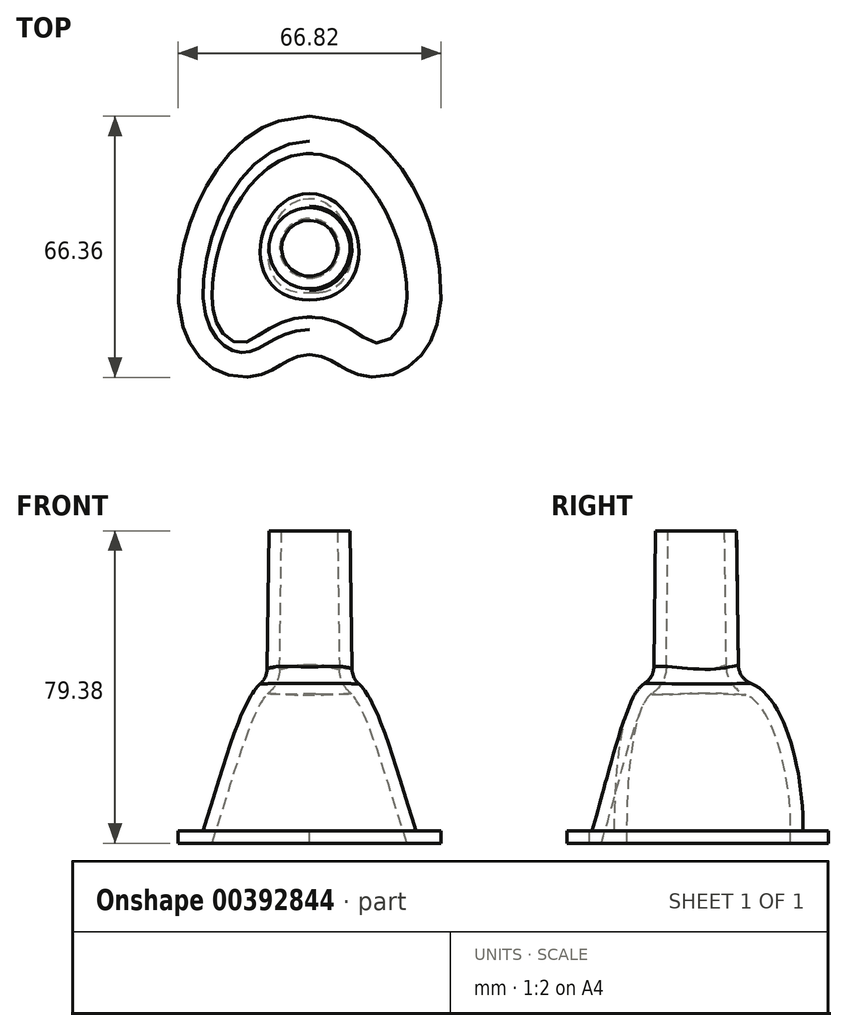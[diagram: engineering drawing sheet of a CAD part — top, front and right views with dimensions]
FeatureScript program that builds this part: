
annotation { "Feature Type Name" : "Feature", "Feature Type Description" : "" }
export const myFeature = defineFeature(function(context is Context, id is Id, definition is map)
    precondition{}
    {
        {
            var Q0;
            Q0=qCreatedBy(makeId("Top.planeOp"),FACE);
            cPlane(context, id + "F0", {"entities" : qUnion([Q0]), "cplaneType" : CPlaneType.OFFSET, "offset" : 76.2 * mm, "width" : 152.4 * mm, "height" : 152.4 * mm});
        }
        {
            var Q0;
            Q0=qCreatedBy(id+"F0.planeOp",FACE);
            var sketch = newSketch(context, id + "F1", { "sketchPlane" : qUnion([Q0])});
            skCircle(sketch, "E0", {"center": v(0, 0) * mm, "radius": 10.29 * mm});
            skSolve(sketch);
        }
        {
            var Q0;
            Q0=qCreatedBy(makeId("Top.planeOp"),FACE);
            cPlane(context, id + "F2", {"entities" : qUnion([Q0]), "cplaneType" : CPlaneType.OFFSET, "offset" : 38.1 * mm, "width" : 152.4 * mm, "height" : 152.4 * mm});
        }
        {
            var Q0;
            Q0=qCreatedBy(id+"F2.planeOp",FACE);
            var sketch = newSketch(context, id + "F3", { "sketchPlane" : qUnion([Q0])});
            skCircle(sketch, "E1", {"center": v(0, 0) * mm, "radius": 10.8 * mm});
            skSolve(sketch);
        }
        {
            var Q0;
            Q0=qCreatedBy(makeId("Top.planeOp"),FACE);
            var sketch = newSketch(context, id + "F4", { "sketchPlane" : qUnion([Q0])});
            skFitSpline(sketch, "E2", {"points": [v(0, 27.2) * mm, v(-26.53, -16.48) * mm, v(-15.51, -26.34) * mm, v(0, -20.7) * mm], "startDerivative": vector(-124.35, 0) * mm, "endDerivative": vector(87.79, 0) * mm});
            skLineSegment(sketch, "E3", {"start": v(0, 27.2) * mm, "end": v(-39.36, 27.2) * mm, "construction": true});
            skLineSegment(sketch, "E4", {"start": v(0, -20.7) * mm, "end": v(-44.27, -20.7) * mm, "construction": true});
            skFitSpline(sketch, "E5.MirrorCS", {"points": [v(0, 27.2) * mm, v(26.53, -16.48) * mm, v(15.51, -26.34) * mm, v(0, -20.7) * mm], "startDerivative": vector(124.35, 0) * mm, "endDerivative": vector(-87.79, 0) * mm});
            skSolve(sketch);
        }
        {
            var Q0;
            Q0=qCreatedBy(makeId("Right.planeOp"),FACE);
            var sketch = newSketch(context, id + "F5", { "sketchPlane" : qUnion([Q0])});
            skPoint(sketch, "E6.0", {"position": v(27.2, 0) * mm});
            skPoint(sketch, "E7.0", {"position": v(-20.7, 0) * mm});
            skLineSegment(sketch, "E8.0", {"start": v(-10.8, 38.1) * mm, "end": v(10.8, 38.1) * mm, "construction": true});
            skFitSpline(sketch, "E9", {"points": [v(10.8, 38.1) * mm, v(27.2, 0) * mm], "startDerivative": vector(31.94, 0) * mm, "endDerivative": vector(0, -52.58) * mm});
            skLineSegment(sketch, "E10", {"start": v(10.8, 38.1) * mm, "end": v(21.44, 38.1) * mm, "construction": true});
            skLineSegment(sketch, "E11", {"start": v(-10.8, 38.1) * mm, "end": v(-18.53, 38.1) * mm, "construction": true});
            skLineSegment(sketch, "E12", {"start": v(27.2, 0) * mm, "end": v(27.2, 17.53) * mm, "construction": true});
            skPoint(sketch, "E13", {"position": v(16.12, 38.1) * mm});
            skFitSpline(sketch, "E14", {"points": [v(-10.8, 38.1) * mm, v(-20.7, 0) * mm], "startDerivative": vector(-23.2, 0) * mm, "endDerivative": vector(0, -52.58) * mm});
            skLineSegment(sketch, "E15", {"start": v(-20.7, 0) * mm, "end": v(-20.7, 17.53) * mm, "construction": true});
            skSolve(sketch);
        }
        {
            var Q0;
            Q0=makeQuery(id+"F3.imprint","IMPRINT",FACE,{"disambiguationData":[TD([[makeQuery(id+"F3.imprint","IMPRINT",EDGE,{"derivedFrom":sQuery(id+"F3.wireOp",EDGE,"E1")}),1.0]])]});
            var Q1;
            Q1=makeQuery(id+"F4.imprint","IMPRINT",FACE,{"disambiguationData":[TD([[makeQuery(id+"F4.imprint","IMPRINT",EDGE,{"derivedFrom":sQuery(id+"F4.wireOp",EDGE,"E2")}),1.0]])]});
            var Q2;
            Q2=sQuery(id+"F5.wireOp",EDGE,"E9");
            var Q3;
            Q3=sQuery(id+"F5.wireOp",EDGE,"E14");
            loft(context, id + "F6", {"addGuides" : true, "sheetProfilesArray" : [{ "sheetProfileEntities" : qUnion([Q0]) }, { "sheetProfileEntities" : qUnion([Q1]) }], "guidesArray" : [{ "guideEntities" : qUnion([Q2]), "guideDerivativeType" : LoftGuideDerivativeType.DEFAULT, "guideDerivativeMagnitude" : 1 }, { "guideEntities" : qUnion([Q3]), "guideDerivativeType" : LoftGuideDerivativeType.DEFAULT, "guideDerivativeMagnitude" : 1 }]});
        }
        {
            var Q0;
            Q0=qCreatedBy(makeId("Top.planeOp"),FACE);
            var sketch = newSketch(context, id + "F7", { "sketchPlane" : qUnion([Q0])});
            skFitSpline(sketch, "E16.0", {"points": [v(0, -27.04) * mm, v(-0.15, -27.04) * mm, v(-0.43, -27.05) * mm, v(-0.85, -27.07) * mm, v(-1.18, -27.1) * mm, v(-1.41, -27.13) * mm, v(-1.54, -27.15) * mm, v(-1.64, -27.16) * mm, v(-1.73, -27.17) * mm, v(-1.84, -27.2) * mm, v(-2.04, -27.23) * mm, v(-2.33, -27.28) * mm, v(-2.61, -27.35) * mm, v(-2.8, -27.4) * mm, v(-2.92, -27.44) * mm, v(-3, -27.46) * mm, v(-3.08, -27.48) * mm, v(-3.18, -27.51) * mm, v(-3.36, -27.57) * mm, v(-3.56, -27.64) * mm, v(-3.77, -27.72) * mm, v(-3.93, -27.78) * mm, v(-4.07, -27.84) * mm, v(-4.16, -27.88) * mm, v(-4.21, -27.9) * mm, v(-4.26, -27.92) * mm, v(-4.3, -27.93) * mm, v(-4.34, -27.95) * mm, v(-4.42, -28) * mm, v(-4.6, -28.07) * mm, v(-4.8, -28.16) * mm, v(-5, -28.27) * mm, v(-5.15, -28.34) * mm, v(-5.26, -28.4) * mm, v(-5.35, -28.45) * mm, v(-5.42, -28.48) * mm, v(-5.47, -28.51) * mm, v(-5.5, -28.53) * mm, v(-5.52, -28.54) * mm, v(-5.54, -28.55) * mm, v(-5.56, -28.56) * mm, v(-5.6, -28.58) * mm, v(-5.65, -28.6) * mm, v(-5.72, -28.65) * mm, v(-5.82, -28.7) * mm, v(-5.95, -28.77) * mm, v(-6.11, -28.87) * mm, v(-6.3, -28.97) * mm, v(-6.48, -29.08) * mm, v(-6.65, -29.18) * mm, v(-6.77, -29.25) * mm, v(-6.84, -29.3) * mm, v(-6.9, -29.33) * mm, v(-6.94, -29.35) * mm, v(-7, -29.4) * mm, v(-7.11, -29.45) * mm, v(-7.27, -29.55) * mm, v(-7.42, -29.64) * mm, v(-7.53, -29.7) * mm, v(-7.6, -29.74) * mm, v(-7.64, -29.77) * mm, v(-7.69, -29.8) * mm, v(-7.76, -29.84) * mm, v(-7.88, -29.91) * mm, v(-8.05, -30.02) * mm, v(-8.23, -30.12) * mm, v(-8.35, -30.19) * mm, v(-8.42, -30.23) * mm, v(-8.46, -30.26) * mm, v(-8.53, -30.3) * mm, v(-8.6, -30.34) * mm, v(-8.71, -30.4) * mm, v(-8.83, -30.46) * mm, v(-9, -30.55) * mm, v(-9.19, -30.66) * mm, v(-9.42, -30.8) * mm, v(-9.66, -30.91) * mm, v(-9.85, -31.01) * mm, v(-10, -31.1) * mm, v(-10.12, -31.15) * mm, v(-10.22, -31.2) * mm, v(-10.29, -31.23) * mm, v(-10.32, -31.25) * mm, v(-10.35, -31.26) * mm, v(-10.39, -31.28) * mm, v(-10.44, -31.3) * mm, v(-10.52, -31.34) * mm, v(-10.64, -31.4) * mm, v(-10.78, -31.46) * mm, v(-10.97, -31.55) * mm, v(-11.2, -31.65) * mm, v(-11.5, -31.77) * mm, v(-11.8, -31.88) * mm, v(-12.1, -31.99) * mm, v(-12.34, -32.08) * mm, v(-12.52, -32.13) * mm, v(-12.62, -32.16) * mm, v(-12.7, -32.19) * mm, v(-12.78, -32.21) * mm, v(-12.9, -32.25) * mm, v(-13.1, -32.3) * mm, v(-13.39, -32.38) * mm, v(-13.74, -32.47) * mm, v(-14.2, -32.57) * mm, v(-14.68, -32.65) * mm, v(-15.17, -32.7) * mm, v(-15.53, -32.74) * mm, v(-15.9, -32.77) * mm, v(-16.4, -32.8) * mm, v(-17.01, -32.8) * mm, v(-17.62, -32.77) * mm, v(-18.11, -32.72) * mm, v(-18.48, -32.68) * mm, v(-18.85, -32.63) * mm, v(-19.34, -32.55) * mm, v(-19.94, -32.42) * mm, v(-20.54, -32.27) * mm, v(-21.02, -32.12) * mm, v(-21.36, -32) * mm, v(-21.72, -31.88) * mm, v(-22.2, -31.7) * mm, v(-22.77, -31.45) * mm, v(-23.34, -31.17) * mm, v(-23.72, -30.96) * mm, v(-23.94, -30.84) * mm, v(-24.1, -30.74) * mm, v(-24.27, -30.64) * mm, v(-24.5, -30.5) * mm, v(-24.87, -30.27) * mm, v(-25.4, -29.9) * mm, v(-25.92, -29.5) * mm, v(-26.27, -29.22) * mm, v(-26.46, -29.05) * mm, v(-26.6, -28.93) * mm, v(-26.76, -28.8) * mm, v(-26.95, -28.62) * mm, v(-27.3, -28.3) * mm, v(-27.76, -27.82) * mm, v(-28.2, -27.32) * mm, v(-28.5, -26.97) * mm, v(-28.67, -26.76) * mm, v(-28.8, -26.6) * mm, v(-28.92, -26.44) * mm, v(-29.09, -26.22) * mm, v(-29.38, -25.83) * mm, v(-29.76, -25.25) * mm, v(-30.13, -24.67) * mm, v(-30.37, -24.25) * mm, v(-30.5, -24) * mm, v(-30.6, -23.82) * mm, v(-30.7, -23.63) * mm, v(-30.83, -23.37) * mm, v(-31.06, -22.92) * mm, v(-31.36, -22.26) * mm, v(-31.63, -21.59) * mm, v(-31.8, -21.1) * mm, v(-31.9, -20.83) * mm, v(-31.97, -20.63) * mm, v(-32.05, -20.41) * mm, v(-32.14, -20.12) * mm, v(-32.3, -19.61) * mm, v(-32.5, -18.88) * mm, v(-32.71, -17.98) * mm, v(-32.9, -17.08) * mm, v(-33.04, -16.15) * mm, v(-33.17, -15.21) * mm, v(-33.26, -14.26) * mm, v(-33.33, -13.28) * mm, v(-33.38, -12.31) * mm, v(-33.4, -11) * mm, v(-33.38, -9.33) * mm, v(-33.25, -7.29) * mm, v(-33.08, -5.57) * mm, v(-32.9, -4.16) * mm, v(-32.73, -3.1) * mm, v(-32.58, -2.23) * mm, v(-32.45, -1.52) * mm, v(-32.34, -1) * mm, v(-32.23, -0.46) * mm, v(-32.08, 0.26) * mm, v(-31.87, 1.15) * mm, v(-31.65, 2.04) * mm, v(-31.46, 2.75) * mm, v(-31.31, 3.28) * mm, v(-31.16, 3.82) * mm, v(-30.95, 4.54) * mm, v(-30.67, 5.44) * mm, v(-30.38, 6.32) * mm, v(-30.16, 6.94) * mm, v(-30.04, 7.3) * mm, v(-29.94, 7.56) * mm, v(-29.85, 7.83) * mm, v(-29.71, 8.18) * mm, v(-29.48, 8.8) * mm, v(-29.13, 9.7) * mm, v(-28.76, 10.56) * mm, v(-28.5, 11.17) * mm, v(-28.35, 11.52) * mm, v(-28.23, 11.77) * mm, v(-28.1, 12.04) * mm, v(-27.95, 12.39) * mm, v(-27.66, 13) * mm, v(-27.24, 13.85) * mm, v(-26.8, 14.7) * mm, v(-26.48, 15.28) * mm, v(-26.3, 15.61) * mm, v(-26.16, 15.86) * mm, v(-26.02, 16.11) * mm, v(-25.82, 16.45) * mm, v(-25.48, 17.03) * mm, v(-24.98, 17.85) * mm, v(-24.47, 18.66) * mm, v(-24.1, 19.2) * mm, v(-23.88, 19.52) * mm, v(-23.72, 19.75) * mm, v(-23.55, 20) * mm, v(-23.33, 20.3) * mm, v(-22.93, 20.86) * mm, v(-22.34, 21.62) * mm, v(-21.74, 22.37) * mm, v(-21.32, 22.88) * mm, v(-21.07, 23.17) * mm, v(-20.88, 23.38) * mm, v(-20.69, 23.6) * mm, v(-20.43, 23.89) * mm, v(-19.97, 24.39) * mm, v(-19.3, 25.08) * mm, v(-18.6, 25.75) * mm, v(-18.11, 26.2) * mm, v(-17.83, 26.46) * mm, v(-17.62, 26.64) * mm, v(-17.4, 26.84) * mm, v(-17.1, 27.1) * mm, v(-16.56, 27.53) * mm, v(-15.8, 28.13) * mm, v(-15, 28.7) * mm, v(-14.45, 29.08) * mm, v(-14.13, 29.3) * mm, v(-13.89, 29.45) * mm, v(-13.63, 29.6) * mm, v(-13.3, 29.81) * mm, v(-12.7, 30.17) * mm, v(-12, 30.55) * mm, v(-11.3, 30.9) * mm, v(-10.76, 31.16) * mm, v(-10.3, 31.37) * mm, v(-10, 31.5) * mm, v(-9.8, 31.58) * mm, v(-9.68, 31.64) * mm, v(-9.53, 31.7) * mm, v(-9.34, 31.77) * mm, v(-9, 31.9) * mm, v(-8.51, 32.09) * mm, v(-7.93, 32.29) * mm, v(-7.14, 32.54) * mm, v(-6.14, 32.81) * mm, v(-4.53, 33.18) * mm, v(-2.48, 33.48) * mm, v(-0.83, 33.56) * mm, v(0, 33.56) * mm]});
            skFitSpline(sketch, "E16.1", {"points": [v(0, 33.56) * mm, v(0.83, 33.56) * mm, v(2.48, 33.48) * mm, v(4.53, 33.18) * mm, v(6.14, 32.81) * mm, v(7.14, 32.54) * mm, v(7.93, 32.29) * mm, v(8.51, 32.09) * mm, v(9, 31.9) * mm, v(9.34, 31.77) * mm, v(9.53, 31.7) * mm, v(9.67, 31.64) * mm, v(9.8, 31.58) * mm, v(10, 31.5) * mm, v(10.3, 31.37) * mm, v(10.76, 31.16) * mm, v(11.3, 30.9) * mm, v(12, 30.55) * mm, v(12.7, 30.17) * mm, v(13.3, 29.81) * mm, v(13.63, 29.6) * mm, v(13.89, 29.45) * mm, v(14.13, 29.3) * mm, v(14.45, 29.08) * mm, v(15, 28.7) * mm, v(15.8, 28.13) * mm, v(16.56, 27.53) * mm, v(17.1, 27.1) * mm, v(17.4, 26.84) * mm, v(17.62, 26.64) * mm, v(17.83, 26.46) * mm, v(18.11, 26.2) * mm, v(18.6, 25.75) * mm, v(19.3, 25.08) * mm, v(19.97, 24.39) * mm, v(20.43, 23.89) * mm, v(20.69, 23.6) * mm, v(20.88, 23.38) * mm, v(21.07, 23.17) * mm, v(21.32, 22.88) * mm, v(21.74, 22.37) * mm, v(22.34, 21.62) * mm, v(22.93, 20.86) * mm, v(23.33, 20.3) * mm, v(23.55, 20) * mm, v(23.72, 19.75) * mm, v(23.88, 19.52) * mm, v(24.1, 19.2) * mm, v(24.47, 18.66) * mm, v(24.98, 17.85) * mm, v(25.48, 17.03) * mm, v(25.82, 16.45) * mm, v(26.02, 16.11) * mm, v(26.16, 15.86) * mm, v(26.3, 15.61) * mm, v(26.48, 15.28) * mm, v(26.8, 14.7) * mm, v(27.24, 13.85) * mm, v(27.66, 13) * mm, v(27.95, 12.39) * mm, v(28.1, 12.04) * mm, v(28.23, 11.77) * mm, v(28.35, 11.52) * mm, v(28.5, 11.17) * mm, v(28.76, 10.57) * mm, v(29.13, 9.7) * mm, v(29.48, 8.8) * mm, v(29.71, 8.19) * mm, v(29.85, 7.83) * mm, v(29.94, 7.56) * mm, v(30.04, 7.3) * mm, v(30.16, 6.94) * mm, v(30.38, 6.32) * mm, v(30.67, 5.44) * mm, v(30.95, 4.54) * mm, v(31.16, 3.82) * mm, v(31.31, 3.28) * mm, v(31.46, 2.75) * mm, v(31.65, 2.04) * mm, v(31.87, 1.15) * mm, v(32.08, 0.26) * mm, v(32.23, -0.46) * mm, v(32.34, -1) * mm, v(32.45, -1.52) * mm, v(32.58, -2.23) * mm, v(32.73, -3.1) * mm, v(32.9, -4.16) * mm, v(33.03, -5.21) * mm, v(33.15, -6.25) * mm, v(33.28, -7.63) * mm, v(33.38, -9.33) * mm, v(33.4, -11) * mm, v(33.38, -12.31) * mm, v(33.33, -13.28) * mm, v(33.26, -14.26) * mm, v(33.17, -15.2) * mm, v(33.04, -16.15) * mm, v(32.9, -17.08) * mm, v(32.71, -17.98) * mm, v(32.5, -18.88) * mm, v(32.3, -19.61) * mm, v(32.14, -20.12) * mm, v(32.05, -20.41) * mm, v(31.97, -20.63) * mm, v(31.9, -20.83) * mm, v(31.8, -21.1) * mm, v(31.63, -21.58) * mm, v(31.36, -22.26) * mm, v(31.06, -22.92) * mm, v(30.83, -23.37) * mm, v(30.7, -23.63) * mm, v(30.6, -23.82) * mm, v(30.5, -24) * mm, v(30.37, -24.24) * mm, v(30.13, -24.66) * mm, v(29.76, -25.25) * mm, v(29.38, -25.83) * mm, v(29.09, -26.22) * mm, v(28.92, -26.44) * mm, v(28.8, -26.6) * mm, v(28.67, -26.76) * mm, v(28.5, -26.97) * mm, v(28.2, -27.32) * mm, v(27.76, -27.82) * mm, v(27.3, -28.3) * mm, v(26.95, -28.61) * mm, v(26.76, -28.8) * mm, v(26.6, -28.93) * mm, v(26.46, -29.05) * mm, v(26.27, -29.22) * mm, v(25.92, -29.5) * mm, v(25.4, -29.9) * mm, v(24.87, -30.27) * mm, v(24.5, -30.5) * mm, v(24.27, -30.64) * mm, v(24.1, -30.74) * mm, v(23.94, -30.84) * mm, v(23.72, -30.96) * mm, v(23.34, -31.17) * mm, v(22.77, -31.45) * mm, v(22.2, -31.7) * mm, v(21.72, -31.88) * mm, v(21.37, -32) * mm, v(21.02, -32.12) * mm, v(20.54, -32.27) * mm, v(19.95, -32.42) * mm, v(19.22, -32.57) * mm, v(18.48, -32.69) * mm, v(17.75, -32.76) * mm, v(17.01, -32.8) * mm, v(16.4, -32.8) * mm, v(15.9, -32.77) * mm, v(15.53, -32.74) * mm, v(15.17, -32.7) * mm, v(14.69, -32.65) * mm, v(14.2, -32.57) * mm, v(13.74, -32.47) * mm, v(13.39, -32.38) * mm, v(13.1, -32.3) * mm, v(12.9, -32.25) * mm, v(12.78, -32.21) * mm, v(12.7, -32.19) * mm, v(12.62, -32.16) * mm, v(12.52, -32.13) * mm, v(12.34, -32.08) * mm, v(12.1, -31.99) * mm, v(11.8, -31.88) * mm, v(11.5, -31.77) * mm, v(11.21, -31.65) * mm, v(10.97, -31.55) * mm, v(10.78, -31.46) * mm, v(10.64, -31.4) * mm, v(10.52, -31.34) * mm, v(10.44, -31.3) * mm, v(10.39, -31.28) * mm, v(10.35, -31.26) * mm, v(10.33, -31.25) * mm, v(10.29, -31.23) * mm, v(10.22, -31.2) * mm, v(10.12, -31.15) * mm, v(10, -31.1) * mm, v(9.85, -31.01) * mm, v(9.66, -30.91) * mm, v(9.42, -30.8) * mm, v(9.19, -30.66) * mm, v(9, -30.55) * mm, v(8.83, -30.47) * mm, v(8.71, -30.4) * mm, v(8.6, -30.34) * mm, v(8.54, -30.3) * mm, v(8.5, -30.28) * mm, v(8.46, -30.26) * mm, v(8.45, -30.24) * mm, v(8.41, -30.23) * mm, v(8.36, -30.2) * mm, v(8.28, -30.15) * mm, v(8.19, -30.1) * mm, v(8.05, -30.02) * mm, v(7.91, -29.93) * mm, v(7.78, -29.86) * mm, v(7.72, -29.82) * mm, v(7.68, -29.8) * mm, v(7.65, -29.78) * mm, v(7.63, -29.76) * mm, v(7.6, -29.74) * mm, v(7.54, -29.7) * mm, v(7.46, -29.66) * mm, v(7.36, -29.6) * mm, v(7.23, -29.53) * mm, v(7.07, -29.43) * mm, v(6.92, -29.34) * mm, v(6.78, -29.26) * mm, v(6.65, -29.18) * mm, v(6.43, -29.05) * mm, v(6.2, -28.91) * mm, v(5.97, -28.79) * mm, v(5.84, -28.71) * mm, v(5.74, -28.66) * mm, v(5.66, -28.62) * mm, v(5.6, -28.58) * mm, v(5.56, -28.56) * mm, v(5.52, -28.54) * mm, v(5.48, -28.51) * mm, v(5.42, -28.48) * mm, v(5.32, -28.43) * mm, v(5.18, -28.36) * mm, v(5.01, -28.27) * mm, v(4.8, -28.17) * mm, v(4.6, -28.07) * mm, v(4.42, -28) * mm, v(4.34, -27.95) * mm, v(4.29, -27.93) * mm, v(4.26, -27.92) * mm, v(4.21, -27.9) * mm, v(4.16, -27.88) * mm, v(4.07, -27.84) * mm, v(3.93, -27.78) * mm, v(3.77, -27.72) * mm, v(3.56, -27.64) * mm, v(3.36, -27.57) * mm, v(3.18, -27.51) * mm, v(3.08, -27.48) * mm, v(3, -27.46) * mm, v(2.92, -27.44) * mm, v(2.8, -27.4) * mm, v(2.61, -27.35) * mm, v(2.33, -27.28) * mm, v(2.04, -27.23) * mm, v(1.84, -27.2) * mm, v(1.72, -27.17) * mm, v(1.64, -27.16) * mm, v(1.54, -27.15) * mm, v(1.41, -27.13) * mm, v(1.18, -27.1) * mm, v(0.85, -27.07) * mm, v(0.43, -27.05) * mm, v(0.15, -27.04) * mm, v(0, -27.04) * mm]});
            skSolve(sketch);
        }
        {
            var Q0;
            Q0 = qSketchRegion(id + "F7", true);
            extrude(context, id + "F8", {"entities" : qUnion([Q0]), "operationType" : NewBodyOperationType.ADD, "oppositeDirection" : true, "depth" : 3.17 * mm});
        }
        {
            var Q1;
            Q1=makeQuery(id+"F1.imprint","IMPRINT",FACE,{"disambiguationData":[TD([[makeQuery(id+"F1.imprint","IMPRINT",EDGE,{"derivedFrom":sQuery(id+"F1.wireOp",EDGE,"E0")}),1.0]])]});
            var Q2;
            Q2=makeQuery(id+"F6.opLoft","CAP_FACE",FACE,{"disambiguationData":[OSD([makeQuery(id+"F3.imprint","IMPRINT",FACE,{"disambiguationData":[TD([[makeQuery(id+"F3.imprint","IMPRINT",EDGE,{"derivedFrom":sQuery(id+"F3.wireOp",EDGE,"E1")}),1.0]])]})])],"isStart":true});
            loft(context, id + "F9", {"operationType" : NewBodyOperationType.ADD, "sheetProfilesArray" : [{ "sheetProfileEntities" : qUnion([Q1]) }, { "sheetProfileEntities" : qUnion([Q2]) }]});
        }
        {
            var Q0;
            Q0=makeQuery(id+"F6.opLoft","MID_CAP_EDGE",EDGE,{"disambiguationData":[OSD([sQuery(id+"F4.wireOp",EDGE,"E5.MirrorCS"),sQuery(id+"F5.wireOp",EDGE,"E9"),sQuery(id+"F5.wireOp",EDGE,"E14")])],"capPos":1.0});
            var Q1;
            {var subQ0=sQuery(id+"F5.wireOp",EDGE,"E14");var subQ1=sQuery(id+"F5.wireOp",EDGE,"E9");var subQ2=sQuery(id+"F3.wireOp",EDGE,"E1");var subQ3=makeQuery(id+"F6.opLoft","MID_CAP_EDGE",EDGE,{"disambiguationData":[OSD([subQ2,subQ1,subQ0]),OD(0.0)],"capPos":0.0});Q1=makeQuery(id+"F9.boolean.opBoolean","MERGE",EDGE,{"derivedFrom":[subQ3,makeQuery(id+"F9.opLoft","MID_CAP_EDGE",EDGE,{"disambiguationData":[OSD([subQ2,subQ1,subQ0]),TDD([makeQuery(id+"F6.opLoft","MID_CAP_VERTEX",VERTEX,{"disambiguationData":[OSD([subQ1])],"capPos":0.0}),makeQuery(id+"F6.opLoft","MID_CAP_VERTEX",VERTEX,{"disambiguationData":[OSD([subQ0])],"capPos":0.0}),subQ3])],"capPos":1.0})]});}
            fillet(context, id + "F10", {"entities" : qUnion([Q0, Q1]), "radius" : 5.08 * mm, "tangentPropagation" : true, "allowEdgeOverflow" : false});
        }
        {
            var Q0;
            Q0=makeQuery(id+"F8.opExtrude","CAP_FACE",FACE,{"disambiguationData":[OSD([sQuery(id+"F7.wireOp",EDGE,"E16.0"),sQuery(id+"F7.wireOp",EDGE,"E16.1")])],"isStart":false});
            var Q1;
            Q1=makeQuery(id+"F9.opLoft","CAP_FACE",FACE,{"disambiguationData":[OSD([makeQuery(id+"F1.imprint","IMPRINT",FACE,{"disambiguationData":[TD([[makeQuery(id+"F1.imprint","IMPRINT",EDGE,{"derivedFrom":sQuery(id+"F1.wireOp",EDGE,"E0")}),1.0]])]})])],"isStart":true});
            shell(context, id + "F11", {"entities" : qUnion([Q0, Q1]), "thickness" : 3.17 * mm});
        }
    });
